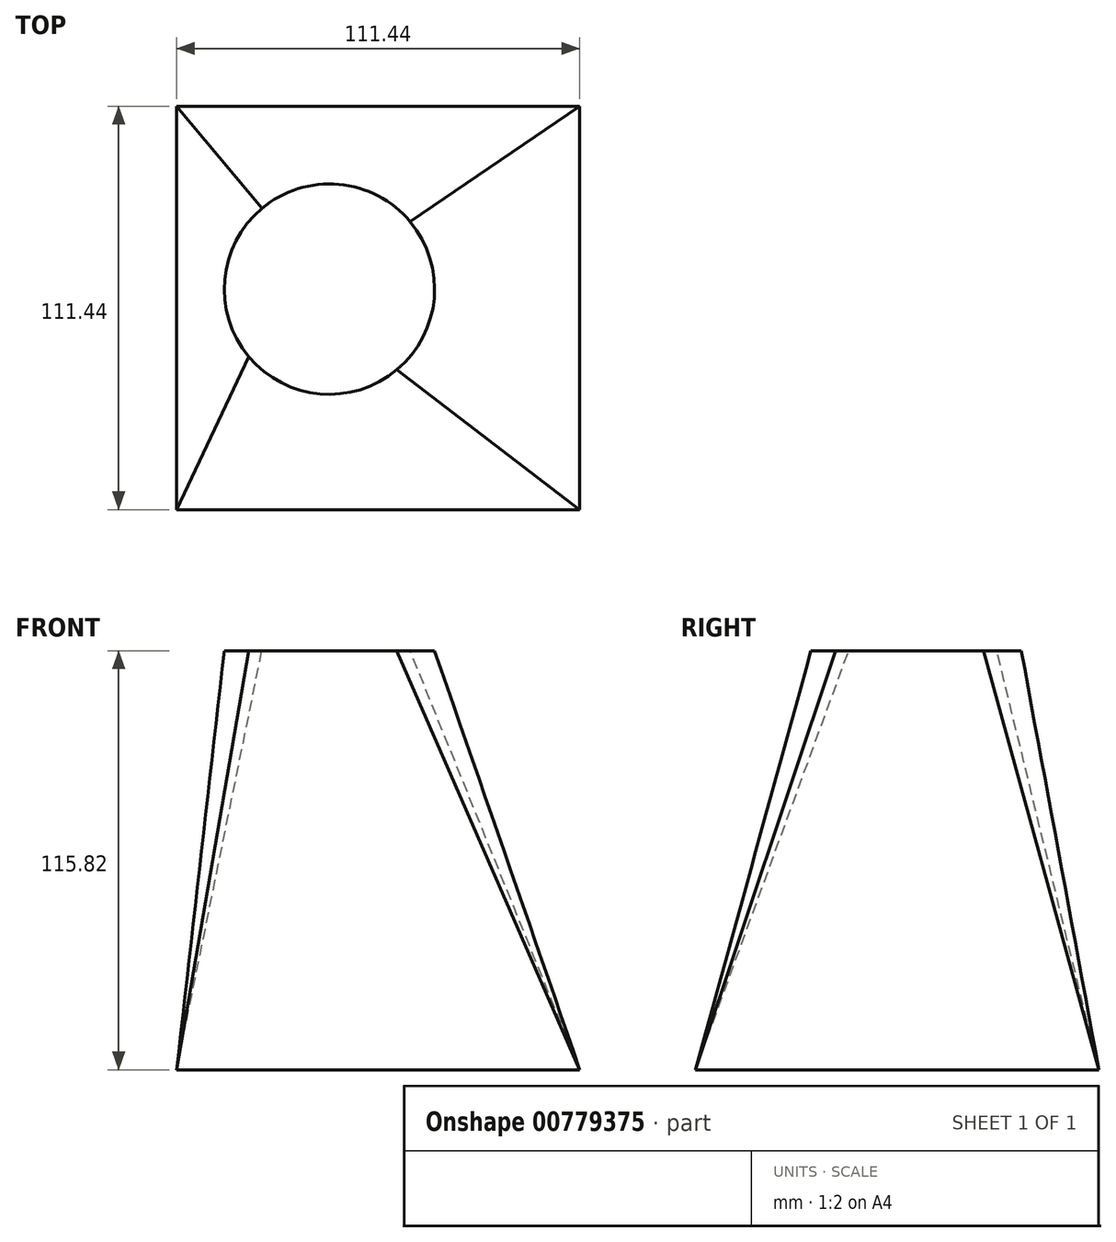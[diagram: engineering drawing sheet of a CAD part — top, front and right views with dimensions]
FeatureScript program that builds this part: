
annotation { "Feature Type Name" : "Feature", "Feature Type Description" : "" }
export const myFeature = defineFeature(function(context is Context, id is Id, definition is map)
    precondition{}
    {
        {
            var Q0;
            Q0=qCreatedBy(makeId("Top.planeOp"),FACE);
            var sketch = newSketch(context, id + "F0", { "sketchPlane" : qUnion([Q0])});
            skLineSegment(sketch, "E0.bottom", {"start": v(-49.02, 65.35) * mm, "end": v(62.42, 65.35) * mm});
            skLineSegment(sketch, "E0.top", {"start": v(-49.02, -46.09) * mm, "end": v(62.42, -46.09) * mm});
            skLineSegment(sketch, "E0.left", {"start": v(-49.02, 65.35) * mm, "end": v(-49.02, -46.09) * mm});
            skLineSegment(sketch, "E0.right", {"start": v(62.42, 65.35) * mm, "end": v(62.42, -46.09) * mm});
            skSolve(sketch);
        }
        {
            var Q0;
            Q0=qCreatedBy(makeId("Top.planeOp"),FACE);
            cPlane(context, id + "F1", {"entities" : qUnion([Q0]), "cplaneType" : CPlaneType.OFFSET, "offset" : 115.82 * mm, "width" : 152.4 * mm, "height" : 152.4 * mm});
        }
        {
            var Q0;
            Q0=qCreatedBy(id+"F1.planeOp",FACE);
            var sketch = newSketch(context, id + "F2", { "sketchPlane" : qUnion([Q0])});
            skCircle(sketch, "E1", {"center": v(-6.78, 14.85) * mm, "radius": 29.07 * mm});
            skSolve(sketch);
        }
        {
            var Q0;
            Q0=makeQuery(id+"F0.imprint","IMPRINT",FACE,{"disambiguationData":[TD([[makeQuery(id+"F0.imprint","IMPRINT",EDGE,{"derivedFrom":sQuery(id+"F0.wireOp",EDGE,"E0.bottom")}),-1.0]])]});
            var Q1;
            Q1=makeQuery(id+"F2.imprint","IMPRINT",FACE,{"disambiguationData":[TD([[makeQuery(id+"F2.imprint","IMPRINT",EDGE,{"derivedFrom":sQuery(id+"F2.wireOp",EDGE,"E1")}),1.0]])]});
            loft(context, id + "F3", {"sheetProfilesArray" : [{ "sheetProfileEntities" : qUnion([Q0]) }, { "sheetProfileEntities" : qUnion([Q1]) }]});
        }
    });
